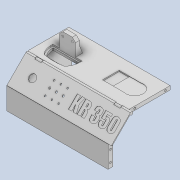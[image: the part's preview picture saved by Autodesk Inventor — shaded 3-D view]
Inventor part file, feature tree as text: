
AUTODESK INVENTOR PART (.ipt)
format: ipt  version: 2022 (Build 260153000, 153)  size: 1,373,696 bytes
history: native  units: mm
features: projected_geometry x52, sketch x38, extrude x35, chamfer x5, plane x3, emboss x1
ambient origin geometry x8: Origin, YZ Plane, XZ Plane, XY Plane, X Axis, Y Axis, Z Axis, Center Point
bodies: Solid1 (feature_tree)
feature tree (134):
  extrude  "Extrusion1"  Depth=120.0mm
  extrude  "Extrusion2"  Depth=40.0mm
  extrude  "Extrusion3"  TaperAngle=135.0deg  [1 undecoded]
  extrude  "Extrusion4"  Depth=125.0mm
  extrude  "Extrusion5"  Depth=1.0mm
  extrude  "Extrusion6"  Depth=20.0mm
  extrude  "Extrusion7"  Depth=10.0mm TaperAngle=0.0deg
  extrude  "Extrusion8"  Depth=0.5mm
  extrude  "Extrusion9"  Depth=0.5mm
  extrude  "Extrusion10"  Depth=0.25mm
  extrude  "Extrusion11"  Depth=0.3mm
  extrude  "Extrusion17"  Depth=20.0mm TaperAngle=0.0deg
  extrude  "Extrusion18"  Depth=14.196mm
  extrude  "Extrusion19"  Depth=0.35mm TaperAngle=0.0deg
  extrude  "Extrusion20"  Depth=19.547688mm
  extrude  "Extrusion21"  Depth=0.3mm
  extrude  "Extrusion22"  Depth=0.3mm
  extrude  "Extrusion23"  Depth=0.3mm
  extrude  "Extrusion24"  Depth=0.3mm
  sketch  "Sketch25"  dims[d73=0.3mm d74=5.0mm d75=0.25mm d76=19.547688mm d77=0.35mm d78=0.0mm]
  chamfer  "Chamfer1"  Distance=20.0mm
  chamfer  "Chamfer2"  Distance=0.35mm
  sketch  "Sketch26"  dims[d79=0.3mm d80=5.0mm d81=0.25mm d82=19.547688mm d83=20.0mm d84=0.0mm]
  extrude  "Extrusion25"  Depth=20.0mm TaperAngle=0.0deg
  emboss  "Emboss1"
  plane  "Work Plane1"
  extrude  "Extrusion26"  Depth=10.0mm TaperAngle=0.0deg
  plane  "Work Plane2"
  extrude  "Extrusion27"  Depth=10.0mm TaperAngle=0.0deg
  plane  "Work Plane3"
  extrude  "Extrusion28"  Depth=10.0mm
  extrude  "Extrusion29"  Depth=10.0mm
  chamfer  "Chamfer3"  Distance=10.0mm
  extrude  "Extrusion30"  Depth=15.0mm
  extrude  "Extrusion31"  Depth=15.0mm
  extrude  "Extrusion32"  Depth=6.0mm
  extrude  "Extrusion33"  Depth=15.0mm
  extrude  "Extrusion34"  Depth=4.2mm
  chamfer  "Chamfer4"  Distance=3.0mm
  chamfer  "Chamfer5"  Distance=4.0mm
  extrude  "Extrusion35"  Depth=10.0mm
  extrude  "Extrusion36"  Depth=10.0mm TaperAngle=0.0deg
  extrude  "Extrusion37"  Depth=10.0mm TaperAngle=45.0deg
  extrude  "Extrusion38"  Depth=10.0mm TaperAngle=45.0deg
  extrude  "Extrusion39"  Depth=10.0mm
  extrude  "Extrusion40"  Depth=10.0mm
  sketch  "Sketch1"  dims[d0=55.0mm d1=120.0mm]
  sketch  "Sketch2"  dims[d2=50.0mm d3=40.0mm]
  projected_geometry  "Projected Loop1"
  sketch  "Sketch3"  dims[d4=135.0deg d5=135.0deg]
  sketch  "Sketch4"  dims[d6=5.0mm d7=125.0mm]
  projected_geometry  "Projected Loop2"
  projected_geometry  "Projected Loop3"
  sketch  "Sketch5"  dims[d8=190.0mm d9=1.0mm]
  sketch  "Sketch6"  dims[d10=1.0mm d11=20.0mm]
  sketch  "Sketch7"  dims[d12=3.0mm d13=10.0mm d14=0.0mm]
  sketch  "Sketch8"  dims[d15=3.0mm d16=0.5mm]
  sketch  "Sketch9"  dims[d18=5.0mm d19=0.5mm]
  sketch  "Sketch10"  dims[d21=0.25mm d22=0.25mm]
  sketch  "Sketch11"  dims[d23=0.0mm d24=0.0mm d25=0.3mm d26=5.0mm d27=0.25mm]
  sketch  "Sketch17"  dims[d28=2.0mm d29=20.0mm d30=0.0mm]
  projected_geometry  "Projected Loop7"
  sketch  "Sketch18"  dims[d36=5.0mm d37=14.196mm]
  sketch  "Sketch19"  dims[d38=0.3mm d39=5.0mm d40=0.25mm d41=0.35mm d42=0.0mm]
  projected_geometry  "Projected Loop8"
  sketch  "Sketch20"  dims[d43=0.3mm d44=5.0mm d45=0.5mm d46=19.547688mm]
  sketch  "Sketch21"  dims[d47=20.0mm d48=0.0mm d49=0.3mm d50=5.0mm d51=0.25mm d52=19.547688mm]
  projected_geometry  "Projected Loop9"
  projected_geometry  "Projected Loop10"
  sketch  "Sketch22"  dims[d53=0.35mm d54=0.0mm d55=0.3mm d56=5.0mm d57=0.25mm d58=19.547688mm]
  projected_geometry  "Projected Loop11"
  projected_geometry  "Projected Loop12"
  projected_geometry  "Projected Loop13"
  projected_geometry  "Projected Loop14"
  sketch  "Sketch23"  dims[d59=228.6mm d60=0.0mm d61=0.3mm d62=5.0mm d63=0.25mm d64=19.547688mm]
  sketch  "Sketch24"  dims[d65=0.35mm d66=0.0mm d67=0.3mm d68=5.0mm d69=0.25mm d70=19.547688mm d71=20.0mm d72=0.0mm]
  projected_geometry  "Projected Loop15"
  projected_geometry  "Projected Loop16"
  projected_geometry  "Projected Loop17"
  projected_geometry  "Projected Loop18"
  projected_geometry  "Projected Loop19"
  projected_geometry  "Projected Loop20"
  sketch  "Sketch27"  dims[d96=3.0mm d107=10.0mm d108=0.0mm]
  sketch  "Sketch28"  dims[d109=12.0mm d110=10.0mm d111=0.0mm]
  sketch  "Sketch29"  dims[d112=10.0mm d113=0.0mm d114=12.0mm]
  sketch  "Sketch30"  dims[d115=5.5mm d116=3.25mm d117=10.0mm d118=0.0mm]
  projected_geometry  "Projected Loop21"
  sketch  "Sketch31"  dims[d119=6.0mm d120=15.0mm]
  projected_geometry  "Projected Loop22"
  sketch  "Sketch32"  dims[d121=6.0mm d122=15.0mm]
  sketch  "Sketch33"  dims[d123=6.0mm d124=6.0mm]
  sketch  "Sketch34"  dims[d125=15.0mm d126=15.0mm]
  projected_geometry  "Projected Loop23"
  sketch  "Sketch35"  dims[d127=4.0mm d128=0.0mm d129=4.2mm]
  sketch  "Sketch36"  dims[d130=4.2mm]
  sketch  "Sketch37"  dims[d131=4.2mm]
  sketch  "Sketch38"  dims[d132=4.2mm d133=3.0mm d134=0.0mm]
  projected_geometry  "Projected Loop24"
  projected_geometry  "Projected Loop25"
  projected_geometry  "Projected Loop26"
  projected_geometry  "Projected Loop27"
  projected_geometry  "Projected Loop28"
  projected_geometry  "Projected Loop29"
  projected_geometry  "Projected Loop30"
  projected_geometry  "Projected Loop31"
  projected_geometry  "Projected Loop32"
  projected_geometry  "Projected Loop33"
  projected_geometry  "Projected Loop34"
  projected_geometry  "Projected Loop35"
  projected_geometry  "Projected Loop36"
  projected_geometry  "Projected Loop37"
  projected_geometry  "Projected Loop38"
  projected_geometry  "Projected Loop39"
  projected_geometry  "Projected Loop40"
  projected_geometry  "Projected Loop41"
  projected_geometry  "Projected Loop42"
  projected_geometry  "Projected Loop43"
  projected_geometry  "Projected Loop44"
  projected_geometry  "Projected Loop45"
  projected_geometry  "Projected Loop46"
  projected_geometry  "Projected Loop47"
  projected_geometry  "Projected Loop48"
  projected_geometry  "Projected Loop49"
  projected_geometry  "Projected Loop50"
  sketch  "Sketch39"  dims[d135=6.0mm]
  projected_geometry  "Projected Loop51"
  sketch  "Sketch40"  dims[d136=6.0mm]
  projected_geometry  "Projected Loop52"
  sketch  "Sketch41"  dims[d137=15.0mm]
  projected_geometry  "Projected Loop53"
  sketch  "Sketch42"  dims[d138=15.0mm d139=4.0mm d140=0.0mm]
  projected_geometry  "Projected Loop54"
  sketch  "Sketch43"  dims[d141=4.2mm d142=4.2mm d143=3.0mm d144=0.0mm d145=2.0mm d146=4.0mm d147=45.0deg d148=2.0mm d149=4.0mm d150=45.0deg d151=22.2mm d152=6.4mm d154=6.4mm d155=6.4mm d156=6.4mm d157=30.0mm d158=40.0mm d159=43.2mm d160=21.4mm d162=21.4mm d163=21.4mm d164=10.0mm d165=13.2mm d166=0.0mm d167=0.0mm d168=5.1mm d170=5.1mm d171=5.1mm d172=5.1mm d173=3.0mm d174=0.0mm d175=22.2mm d176=6.4mm d177=6.4mm d178=6.4mm d179=6.4mm d180=6.4mm d181=30.0mm d182=40.0mm d183=43.2mm d184=21.4mm d185=21.4mm d186=21.4mm d187=21.4mm d188=10.0mm d189=13.2mm d190=0.0mm d191=0.0mm d192=5.1mm d193=5.1mm d194=5.1mm d195=5.1mm d196=5.1mm d197=1.0mm d198=0.0mm d200=50.0mm d201=6.0mm d202=10.0mm d203=3.0mm d204=10.0mm d205=0.0mm d206=160.0mm d207=10.0mm d208=0.0mm d209=266.0mm d210=10.0mm d211=0.0mm d212=6.0mm d213=6.0mm d214=6.0mm d215=10.0mm d216=0.0mm d217=10.0mm d218=4.0mm d219=45.0deg d299=27.0mm d300=67.21989mm d301=67.21989mm d302=52.0mm d303=74.5mm d304=26.0mm d305=26.0mm d306=121.0mm d307=0.25mm d308=0.25mm d309=0.25mm d310=0.25mm d311=3.5mm d312=0.0mm d313=32.75mm d314=2.5mm d315=0.0mm d316=72.0mm d317=91.999999mm d318=81.999999mm d319=167.166667mm d320=45.750001mm d321=45.750001mm d322=50.750001mm d323=172.166667mm d324=50.750001mm d325=7.0mm d326=7.0mm d327=2.0mm d328=2.0mm d329=5.0mm d330=32.384967mm d331=32.384967mm d332=22.0mm d333=0.15mm d334=5.0mm d335=0.0mm d336=72.0mm d337=91.999999mm d338=81.999999mm d339=167.166667mm d340=45.750001mm d341=45.750001mm d342=50.750001mm d343=172.166667mm d344=50.750001mm d345=7.0mm d346=7.0mm d347=2.0mm d348=2.0mm d349=5.0mm d350=32.384967mm d351=32.384967mm d352=22.0mm d353=0.15mm d354=5.0mm d355=0.0mm d356=50.0mm d357=21.15mm d358=50.0mm d359=0.0mm d360=10.0mm d361=25.0mm d362=45.0deg d363=10.0mm d364=25.0mm d365=45.0deg d366=50.0mm d367=12.5mm d368=5.5mm d369=5.5mm d370=15.0mm d371=15.0mm d372=0.0mm d373=0.0mm d375=0.5mm d376=5.347759mm d377=9.695518mm d378=9.445518mm d379=0.25mm d380=10.195518mm d381=10.695518mm d382=20.0mm d383=0.0mm d384=22.2mm d385=21.0mm d386=32.0mm d387=60.0mm d388=0.25mm d389=0.0mm d390=0.25mm d391=0.0mm d392=0.25mm d393=0.0mm d394=0.25mm d395=0.0mm d17=0.872665mm]
  projected_geometry  "Projected Loop55"
note: 1 required parameter value undecoded (feature->parameter linkage not recoverable at this tier; creation-order binding heuristic only, values carry confidence <= 0.55)
